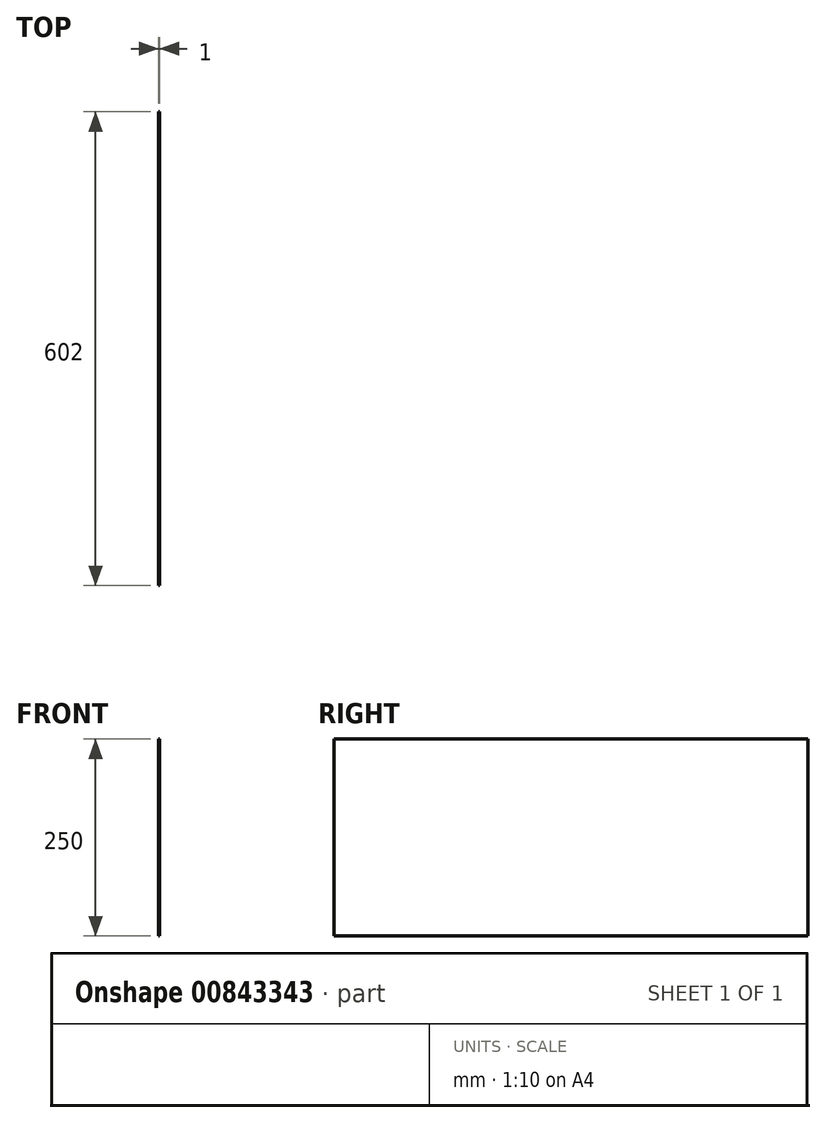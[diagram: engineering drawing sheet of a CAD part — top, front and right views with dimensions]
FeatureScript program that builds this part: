
annotation { "Feature Type Name" : "Feature", "Feature Type Description" : "" }
export const myFeature = defineFeature(function(context is Context, id is Id, definition is map)
    precondition{}
    {
        {
            var Q0;
            Q0=qCreatedBy(makeId("Right.planeOp"),FACE);
            var sketch = newSketch(context, id + "F0", { "sketchPlane" : qUnion([Q0])});
            skLineSegment(sketch, "E0.bottom", {"start": v(301, 125) * mm, "end": v(-301, 125) * mm});
            skLineSegment(sketch, "E0.top", {"start": v(301, -125) * mm, "end": v(-301, -125) * mm});
            skLineSegment(sketch, "E0.left", {"start": v(301, 125) * mm, "end": v(301, -125) * mm});
            skLineSegment(sketch, "E0.right", {"start": v(-301, 125) * mm, "end": v(-301, -125) * mm});
            skPoint(sketch, "E0.middle", {"position": v(0, 0) * mm});
            skSolve(sketch);
        }
        {
            var Q0;
            Q0 = qSketchRegion(id + "F0", true);
            extrude(context, id + "F1", {"entities" : qUnion([Q0]), "depth" : 1 * mm, "offsetDistance" : 25 * mm});
        }
    });
